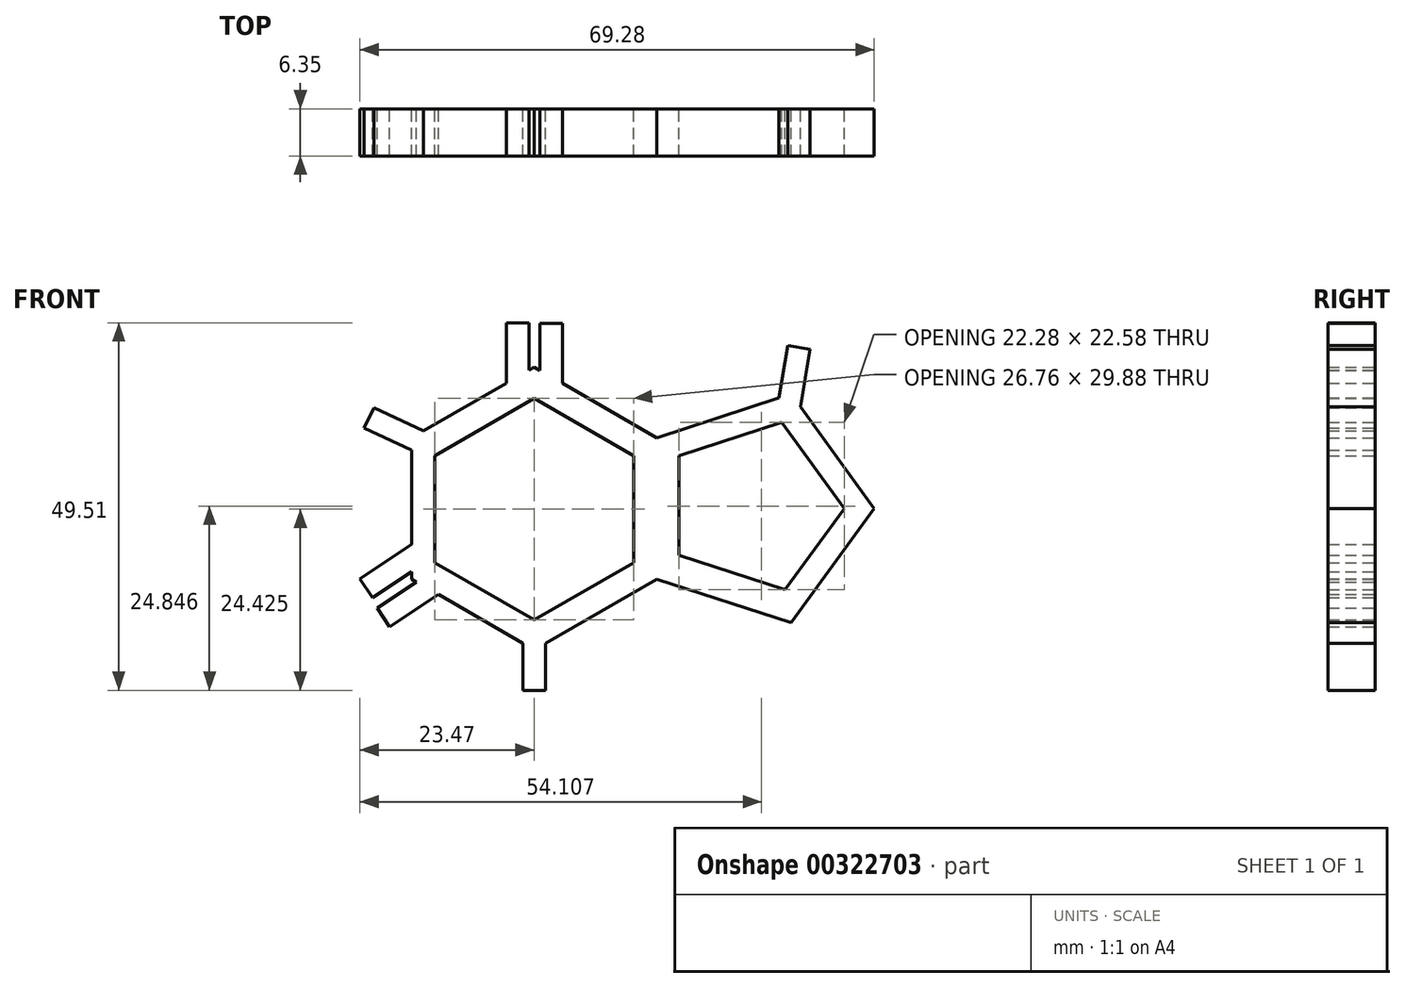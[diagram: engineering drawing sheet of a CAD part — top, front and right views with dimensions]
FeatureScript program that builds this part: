
annotation { "Feature Type Name" : "Feature", "Feature Type Description" : "" }
export const myFeature = defineFeature(function(context is Context, id is Id, definition is map)
    precondition{}
    {
        {
            var Q0;
            Q0=qCreatedBy(makeId("Front.planeOp"),FACE);
            var sketch = newSketch(context, id + "F0", { "sketchPlane" : qUnion([Q0])});
            skLineSegment(sketch, "E0", {"start": v(0, 19.05) * mm, "end": v(16.5, 9.52) * mm});
            skLineSegment(sketch, "E1", {"start": v(16.5, 9.53) * mm, "end": v(16.5, 0) * mm});
            skLineSegment(sketch, "E2.MirrorCS", {"start": v(16.5, -9.53) * mm, "end": v(16.5, 0) * mm});
            skLineSegment(sketch, "E3.MirrorCS", {"start": v(0, -19.05) * mm, "end": v(16.5, -9.52) * mm});
            skLineSegment(sketch, "E4.MirrorCS", {"start": v(0, 19.05) * mm, "end": v(-16.5, 9.52) * mm});
            skLineSegment(sketch, "E5.MirrorCS", {"start": v(-16.5, 9.53) * mm, "end": v(-16.5, 0) * mm});
            skLineSegment(sketch, "E6.MirrorCS", {"start": v(-16.5, -9.53) * mm, "end": v(-16.5, 0) * mm});
            skLineSegment(sketch, "E7.MirrorCS", {"start": v(0, -19.05) * mm, "end": v(-16.5, -9.52) * mm});
            skLineSegment(sketch, "E8", {"start": v(16.5, 9.52) * mm, "end": v(34.62, 15.41) * mm});
            skLineSegment(sketch, "E9", {"start": v(34.62, 15.41) * mm, "end": v(45.81, 0) * mm});
            skLineSegment(sketch, "E10", {"start": v(16.5, 0) * mm, "end": v(45.81, 0) * mm, "construction": true});
            skLineSegment(sketch, "E11.MirrorCS", {"start": v(34.62, -15.41) * mm, "end": v(45.81, 0) * mm});
            skLineSegment(sketch, "E12.MirrorCS", {"start": v(16.5, -9.53) * mm, "end": v(34.62, -15.41) * mm});
            skLineSegment(sketch, "E13", {"start": v(0, -24.52) * mm, "end": v(1.52, -24.52) * mm});
            skLineSegment(sketch, "E14", {"start": v(1.52, -24.52) * mm, "end": v(1.52, -18.17) * mm});
            skLineSegment(sketch, "E15.MirrorCS", {"start": v(-1.52, -24.52) * mm, "end": v(-1.52, -18.17) * mm});
            skLineSegment(sketch, "E16.MirrorCS", {"start": v(0, -24.52) * mm, "end": v(-1.52, -24.52) * mm});
            skLineSegment(sketch, "E17", {"start": v(0.76, 18.61) * mm, "end": v(0.76, 24.96) * mm});
            skLineSegment(sketch, "E18", {"start": v(0.76, 24.96) * mm, "end": v(3.81, 24.96) * mm});
            skLineSegment(sketch, "E19", {"start": v(3.81, 24.96) * mm, "end": v(3.81, 16.85) * mm});
            skLineSegment(sketch, "E20.MirrorCS", {"start": v(-0.71, 18.64) * mm, "end": v(-0.71, 24.99) * mm});
            skLineSegment(sketch, "E21.MirrorCS", {"start": v(-0.71, 24.99) * mm, "end": v(-3.76, 24.99) * mm});
            skLineSegment(sketch, "E22.MirrorCS", {"start": v(-3.76, 24.99) * mm, "end": v(-3.76, 16.88) * mm});
            skLineSegment(sketch, "E23", {"start": v(35.67, 21.67) * mm, "end": v(37.17, 21.42) * mm});
            skLineSegment(sketch, "E24", {"start": v(37.17, 21.42) * mm, "end": v(35.87, 13.69) * mm});
            skLineSegment(sketch, "E25", {"start": v(35.67, 21.67) * mm, "end": v(34.17, 21.93) * mm});
            skLineSegment(sketch, "E26", {"start": v(34.17, 21.93) * mm, "end": v(32.98, 14.88) * mm});
            skLineSegment(sketch, "E27", {"start": v(-22.25, 12.21) * mm, "end": v(-21.6, 13.6) * mm});
            skLineSegment(sketch, "E28", {"start": v(-21.6, 13.6) * mm, "end": v(-14.89, 10.45) * mm});
            skLineSegment(sketch, "E29", {"start": v(-22.25, 12.21) * mm, "end": v(-22.9, 10.83) * mm});
            skLineSegment(sketch, "E30", {"start": v(-22.9, 10.83) * mm, "end": v(-16.5, 7.84) * mm});
            skLineSegment(sketch, "E31", {"start": v(-15.84, -9.9) * mm, "end": v(-21.14, -13.41) * mm});
            skLineSegment(sketch, "E32", {"start": v(-21.14, -13.41) * mm, "end": v(-19.45, -15.95) * mm});
            skLineSegment(sketch, "E33", {"start": v(-19.45, -15.95) * mm, "end": v(-12.9, -11.6) * mm});
            skLineSegment(sketch, "E34", {"start": v(-16.5, -8.53) * mm, "end": v(-21.8, -12.03) * mm});
            skLineSegment(sketch, "E35", {"start": v(-21.8, -12.03) * mm, "end": v(-23.47, -9.5) * mm});
            skLineSegment(sketch, "E36", {"start": v(-23.47, -9.5) * mm, "end": v(-16.5, -4.87) * mm});
            skSolve(sketch);
        }
        {
            var Q0;
            Q0 = qSketchRegion(id + "F0", true);
            extrude(context, id + "F1", {"entities" : qUnion([Q0]), "depth" : 6.35 * mm});
        }
        {
            var Q0;
            {var subQ13=sQuery(id+"F0.wireOp",EDGE,"E1");Q0=makeQuery(id+"F0.imprint","IMPRINT",FACE,{"disambiguationData":[TD([[makeQuery(id+"F0.imprint","IMPRINT",EDGE,{"derivedFrom":subQ13}),-1.0]])]});}
            var sketch = newSketch(context, id + "F2", { "sketchPlane" : qUnion([Q0])});
            skLineSegment(sketch, "E37", {"start": v(0, 14.84) * mm, "end": v(-13.38, 7.12) * mm});
            skLineSegment(sketch, "E38", {"start": v(-13.38, 7.12) * mm, "end": v(-13.38, -7.3) * mm});
            skLineSegment(sketch, "E39", {"start": v(-13.38, -7.3) * mm, "end": v(0, -15.04) * mm});
            skLineSegment(sketch, "E40", {"start": v(0, -15.04) * mm, "end": v(13.38, -7.3) * mm});
            skLineSegment(sketch, "E41", {"start": v(13.38, -7.3) * mm, "end": v(13.38, 7.12) * mm});
            skLineSegment(sketch, "E42", {"start": v(13.38, 7.12) * mm, "end": v(0, 14.84) * mm});
            skLineSegment(sketch, "E43", {"start": v(19.5, -6.31) * mm, "end": v(19.5, 7.12) * mm});
            skLineSegment(sketch, "E44", {"start": v(19.5, 7.12) * mm, "end": v(33.34, 11.62) * mm});
            skLineSegment(sketch, "E45", {"start": v(33.34, 11.62) * mm, "end": v(41.78, 0) * mm});
            skLineSegment(sketch, "E46", {"start": v(41.78, 0) * mm, "end": v(33.81, -10.96) * mm});
            skLineSegment(sketch, "E47", {"start": v(33.81, -10.96) * mm, "end": v(19.5, -6.31) * mm});
            skSolve(sketch);
        }
        {
            var Q0;
            Q0 = qSketchRegion(id + "F2", true);
            extrude(context, id + "F3", {"entities" : qUnion([Q0]), "operationType" : NewBodyOperationType.REMOVE, "depth" : 60.96 * mm});
        }
    });
